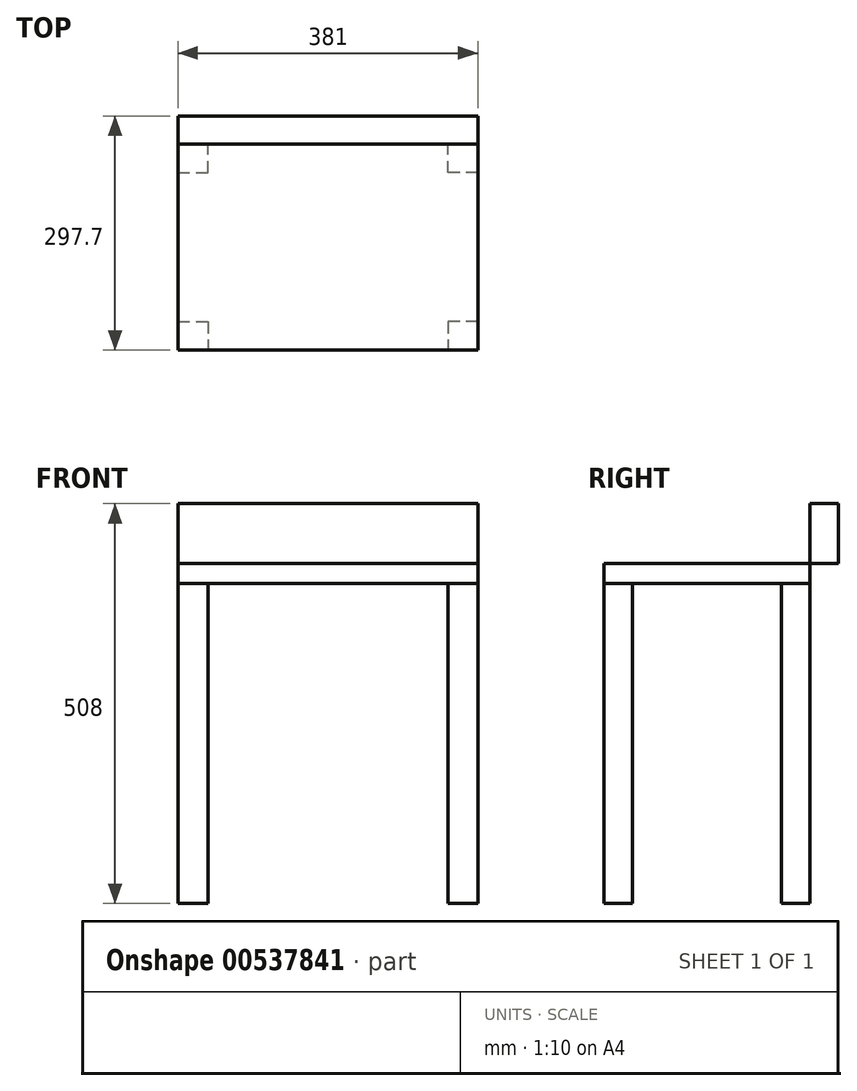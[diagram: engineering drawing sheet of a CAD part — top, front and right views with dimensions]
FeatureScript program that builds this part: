
annotation { "Feature Type Name" : "Feature", "Feature Type Description" : "" }
export const myFeature = defineFeature(function(context is Context, id is Id, definition is map)
    precondition{}
    {
        {
            var Q0;
            Q0=qCreatedBy(makeId("Top.planeOp"),FACE);
            var sketch = newSketch(context, id + "F0", { "sketchPlane" : qUnion([Q0])});
            skLineSegment(sketch, "E0", {"start": v(0, 0) * mm, "end": v(0, 36.33) * mm});
            skLineSegment(sketch, "E1", {"start": v(0, 36.33) * mm, "end": v(38.1, 36.33) * mm});
            skLineSegment(sketch, "E2", {"start": v(38.1, 36.33) * mm, "end": v(38.1, 0) * mm});
            skLineSegment(sketch, "E3", {"start": v(38.1, 0) * mm, "end": v(0, 0) * mm});
            skLineSegment(sketch, "E4", {"start": v(38.1, 3.9) * mm, "end": v(342.9, 3.9) * mm});
            skLineSegment(sketch, "E5", {"start": v(38.1, 0) * mm, "end": v(342.9, 0) * mm});
            skLineSegment(sketch, "E6", {"start": v(342.9, 3.9) * mm, "end": v(342.9, 0) * mm});
            skLineSegment(sketch, "E7", {"start": v(190.5, 3.9) * mm, "end": v(190.5, 257.9) * mm});
            skLineSegment(sketch, "E8.MirrorCS", {"start": v(381, 36.33) * mm, "end": v(342.9, 36.33) * mm});
            skLineSegment(sketch, "E9.MirrorCS", {"start": v(381, 0) * mm, "end": v(381, 36.33) * mm});
            skLineSegment(sketch, "E10.MirrorCS", {"start": v(342.9, 36.33) * mm, "end": v(342.9, 0) * mm});
            skLineSegment(sketch, "E11.MirrorCS", {"start": v(342.9, 0) * mm, "end": v(381, 0) * mm});
            skLineSegment(sketch, "E12", {"start": v(190.5, 130.9) * mm, "end": v(151.42, 130.9) * mm});
            skPoint(sketch, "E12.endSnap0", {"position": v(190.5, 130.9) * mm});
            skLineSegment(sketch, "E13.MirrorCS", {"start": v(381, 225.48) * mm, "end": v(342.9, 225.48) * mm});
            skLineSegment(sketch, "E14.MirrorCS", {"start": v(342.9, 261.81) * mm, "end": v(381, 261.81) * mm});
            skLineSegment(sketch, "E15.MirrorCS", {"start": v(381, 261.81) * mm, "end": v(381, 225.48) * mm});
            skLineSegment(sketch, "E16.MirrorCS", {"start": v(342.9, 225.48) * mm, "end": v(342.9, 261.81) * mm});
            skLineSegment(sketch, "E17.MirrorCS", {"start": v(0, 261.81) * mm, "end": v(0, 225.48) * mm});
            skLineSegment(sketch, "E18.MirrorCS", {"start": v(0, 225.48) * mm, "end": v(38.1, 225.48) * mm});
            skLineSegment(sketch, "E19.MirrorCS", {"start": v(38.1, 225.48) * mm, "end": v(38.1, 261.81) * mm});
            skLineSegment(sketch, "E20.MirrorCS", {"start": v(38.1, 261.81) * mm, "end": v(0, 261.81) * mm});
            skLineSegment(sketch, "E21.MirrorCS", {"start": v(38.1, 261.81) * mm, "end": v(342.9, 261.81) * mm});
            skLineSegment(sketch, "E22.MirrorCS", {"start": v(38.1, 257.9) * mm, "end": v(342.9, 257.9) * mm});
            skSolve(sketch);
        }
        {
            var Q0;
            Q0=makeQuery(id+"F0.imprint","IMPRINT",FACE,{"disambiguationData":[TD([[makeQuery(id+"F0.imprint","IMPRINT",EDGE,{"derivedFrom":sQuery(id+"F0.wireOp",EDGE,"E0")}),-1.0]])]});
            var Q1;
            Q1=makeQuery(id+"F0.imprint","IMPRINT",FACE,{"disambiguationData":[TD([[makeQuery(id+"F0.imprint","IMPRINT",EDGE,{"derivedFrom":sQuery(id+"F0.wireOp",EDGE,"E17.MirrorCS")}),1.0]])]});
            var Q2;
            {var subQ1=sQuery(id+"F0.wireOp",EDGE,"E13.MirrorCS");Q2=makeQuery(id+"F0.imprint","IMPRINT",FACE,{"disambiguationData":[TD([[makeQuery(id+"F0.imprint","IMPRINT",EDGE,{"derivedFrom":subQ1}),-1.0]])]});}
            var Q3;
            {var subQ3=sQuery(id+"F0.wireOp",EDGE,"E8.MirrorCS");Q3=makeQuery(id+"F0.imprint","IMPRINT",FACE,{"disambiguationData":[TD([[makeQuery(id+"F0.imprint","IMPRINT",EDGE,{"derivedFrom":subQ3}),1.0]])]});}
            extrude(context, id + "F1", {"entities" : qUnion([Q0, Q1, Q2, Q3]), "depth" : 406.4 * mm, "offsetDistance" : 25.4 * mm});
        }
        {
            var Q0;
            Q0=makeQuery(id+"F1.opExtrude","CAP_FACE",FACE,{"disambiguationData":[OSD([sQuery(id+"F0.wireOp",EDGE,"E8.MirrorCS"),sQuery(id+"F0.wireOp",EDGE,"E9.MirrorCS"),sQuery(id+"F0.wireOp",EDGE,"E10.MirrorCS"),sQuery(id+"F0.wireOp",EDGE,"E11.MirrorCS")])],"isStart":false});
            var sketch = newSketch(context, id + "F2", { "sketchPlane" : qUnion([Q0])});
            skLineSegment(sketch, "E23.bottom", {"start": v(0, 0) * mm, "end": v(381, 0) * mm});
            skLineSegment(sketch, "E23.top", {"start": v(0, 261.81) * mm, "end": v(381, 261.81) * mm});
            skLineSegment(sketch, "E23.left", {"start": v(0, 0) * mm, "end": v(0, 261.81) * mm});
            skLineSegment(sketch, "E23.right", {"start": v(381, 0) * mm, "end": v(381, 261.81) * mm});
            skSolve(sketch);
        }
        {
            var Q0;
            Q0 = qSketchRegion(id + "F2", true);
            extrude(context, id + "F3", {"entities" : qUnion([Q0]), "depth" : 25.4 * mm, "offsetDistance" : 25.4 * mm});
        }
        {
            var Q0;
            Q0=makeQuery(id+"F3.opExtrude","CAP_FACE",FACE,{"disambiguationData":[OSD([sQuery(id+"F2.wireOp",EDGE,"E23.bottom"),sQuery(id+"F2.wireOp",EDGE,"E23.top"),sQuery(id+"F2.wireOp",EDGE,"E23.left"),sQuery(id+"F2.wireOp",EDGE,"E23.right")])],"isStart":false});
            var sketch = newSketch(context, id + "F4", { "sketchPlane" : qUnion([Q0])});
            skLineSegment(sketch, "E24", {"start": v(0, 261.81) * mm, "end": v(0, 297.7) * mm});
            skLineSegment(sketch, "E25", {"start": v(0, 297.7) * mm, "end": v(381, 297.7) * mm});
            skLineSegment(sketch, "E26", {"start": v(381, 297.7) * mm, "end": v(381, 261.81) * mm});
            skSolve(sketch);
        }
        {
            var Q0;
            Q0 = qSketchRegion(id + "F4", true);
            var Q1;
            Q1=makeQuery(id+"F4.imprint","IMPRINT",FACE,{"disambiguationData":[TD([[makeQuery(id+"F4.imprint","IMPRINT",EDGE,{"derivedFrom":sQuery(id+"F4.wireOp",EDGE,"E24")}),-1.0]])]});
            extrude(context, id + "F5", {"entities" : qUnion([Q0, Q1]), "depth" : 76.2 * mm, "offsetDistance" : 25.4 * mm});
        }
    });
